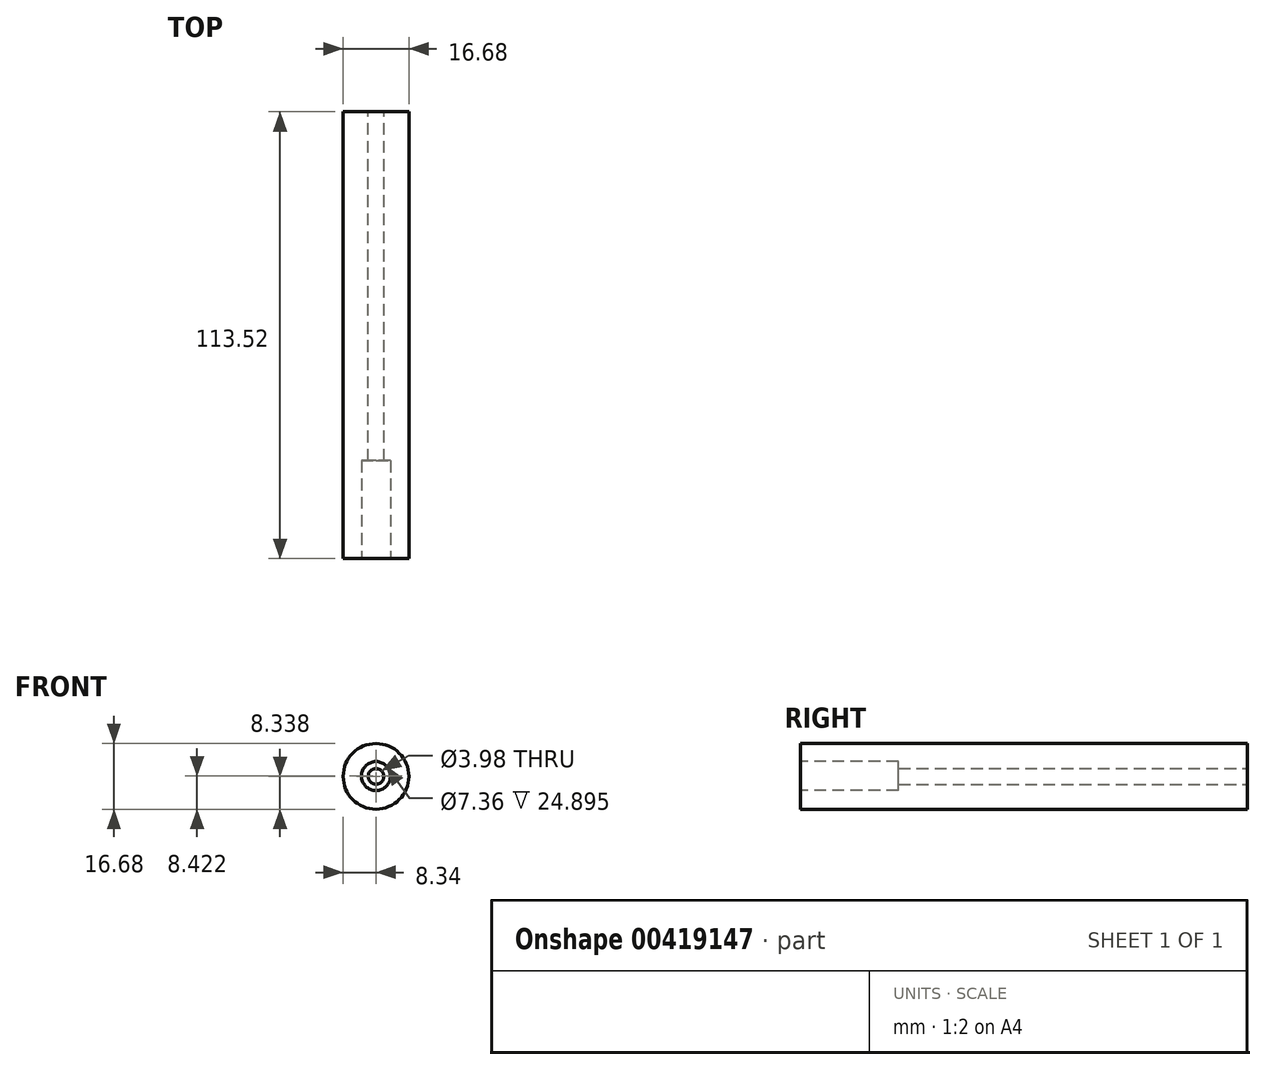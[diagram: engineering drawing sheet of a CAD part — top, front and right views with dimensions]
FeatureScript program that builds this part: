
annotation { "Feature Type Name" : "Feature", "Feature Type Description" : "" }
export const myFeature = defineFeature(function(context is Context, id is Id, definition is map)
    precondition{}
    {
        {
            var Q0;
            Q0=qCreatedBy(makeId("Right.planeOp"),FACE);
            var sketch = newSketch(context, id + "F0", { "sketchPlane" : qUnion([Q0])});
            skPoint(sketch, "E0.start.orphan", {"position": v(-47.76, 0) * mm});
            skLineSegment(sketch, "E1", {"start": v(-47.76, 0) * mm, "end": v(65.76, 0) * mm});
            skLineSegment(sketch, "E2", {"start": v(65.76, 6.35) * mm, "end": v(-43.8, 6.35) * mm});
            skLineSegment(sketch, "E3", {"start": v(-47.76, 0) * mm, "end": v(-47.76, 8.34) * mm});
            skLineSegment(sketch, "E4", {"start": v(-43.8, 8.34) * mm, "end": v(-43.8, 6.35) * mm});
            skLineSegment(sketch, "E5", {"start": v(65.76, 6.35) * mm, "end": v(65.76, 0) * mm});
            skPoint(sketch, "E6.startSnap0", {"position": v(-43.8, 10.33) * mm});
            skPoint(sketch, "E7.orphan", {"position": v(-43.8, 14.3) * mm});
            skLineSegment(sketch, "E8", {"start": v(-43.8, 8.34) * mm, "end": v(-47.76, 8.34) * mm});
            skPoint(sketch, "E6.end.orphan", {"position": v(-43.8, 10.33) * mm});
            skPoint(sketch, "E9.orphan", {"position": v(-47.76, 10.33) * mm});
            skSolve(sketch);
        }
        {
            var Q0;
            Q0=makeQuery(id+"F0.imprint","IMPRINT",FACE,{"disambiguationData":[TD([[makeQuery(id+"F0.imprint","IMPRINT",EDGE,{"derivedFrom":sQuery(id+"F0.wireOp",EDGE,"E1")}),1.0]])]});
            var Q1;
            Q1=sQuery(id+"F0.wireOp",EDGE,"E8");
            revolve(context, id + "F1", {"entities" : qUnion([Q0]), "axis" : qUnion([Q1]), "revolveType" : RevolveType.FULL});
        }
        {
            var Q0;
            Q0=qCreatedBy(makeId("Front.planeOp"),FACE);
            cPlane(context, id + "F2", {"entities" : qUnion([Q0]), "cplaneType" : CPlaneType.OFFSET, "offset" : 48.26 * mm, "width" : 152.4 * mm, "height" : 152.4 * mm});
        }
        {
            var Q0;
            Q0=qCreatedBy(id+"F2.planeOp",FACE);
            var sketch = newSketch(context, id + "F3", { "sketchPlane" : qUnion([Q0])});
            skLineSegment(sketch, "E10", {"start": v(0, 0) * mm, "end": v(0, 16.84) * mm});
            skLineSegment(sketch, "E11", {"start": v(0, 0) * mm, "end": v(0, 8.42) * mm});
            skCircle(sketch, "E12", {"center": v(0, 8.42) * mm, "radius": 3.68 * mm});
            skSolve(sketch);
        }
        {
            var Q0;
            Q0 = qSketchRegion(id + "F3", true);
            extrude(context, id + "F4", {"entities" : qUnion([Q0]), "operationType" : NewBodyOperationType.REMOVE, "oppositeDirection" : true, "depth" : 25.4 * mm});
        }
    });
